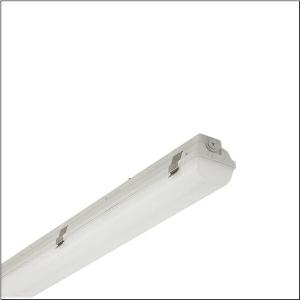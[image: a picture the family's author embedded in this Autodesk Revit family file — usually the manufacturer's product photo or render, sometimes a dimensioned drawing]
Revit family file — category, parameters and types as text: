
# Revit family: monsun_r__21_eco_51fj20ml45a_05e8
name_source: partatom
category: Lighting Fixtures
units: mm (PartAtom-declared; Revit-internal decimal feet)

## family parameters
Cut with Voids When Loaded = No
Host = Face
Light Source = No
Part Type = Normal
Room Calculation Point = No
Round Connector Dimension = Use Diameter
Shared = No

## types (1)
- --- (1 x LED, 4900 lm, 36 W, 4000K)
    Apparent Load = 36 VA
    CIE Flux Codes = 40 69 88 88 100
    Color Rendering = 80
    Color Temperature = 4000K
    Default Elevation = 1800 mm
    Description = Monsun® 21 Eco, damp-proof luminaire, primary optical cover: diffuser, of PC, UV-stabilised, frosted, light emission: direct distribution, primary light characteristic: symmetric, installation type: suspended mounting, surface-mounted, LED, rated luminous flux: 4.900lm, luminous efficacy: 132lm/W, light colour: 840, colour temperature: 4000K, control gear: ECG Multilumen, with terminal, 3-pole, max. 2.5mm², mains connection: 220..240V, AC, 50/60Hz, rated input power: 36W, housing, of glass-fibre reinforced polyester, light grey (RAL 7035), length: 1.277mm, width: 90mm, height: 95mm, clip for enclosure, of spring steel V2A, protection rating (complete): IP66, insulation class (complete): insulation class I (protective earthing), certification: CE, UKCA, protection symbol: D, impact resistance: IK08, permissible operating ambient temperature: -20..+35°C, corresponds to IFS (International Featured Standards) requirements for safety and quality in the food industry, contact your sales advisor before using the luminaires in applications with unclear chemical exposure, large temperature fluctuations or condensation-forming humidity, packaging unit: 1 piece
    Height = 103 mm
    Lamp = 1 x LED
    Lamp Light Flux = 4900 lm
    Lamp Power = 36 W
    Lamp count = 1
    Length = 1277 mm
    Luminous efficacy = 136 lm/W
    Manufacturer = Siteco
    ModVariant = No
    Model = 51FJ20ML45A
    Mounting Place = Ceiling
    Mounting Type = Surface mounted
    Number of Poles = 1
    OnlyDefault = Yes
    Power Factor = 1
    Product Name = Monsun® 21 Eco
    Product group = damp-proof luminaire
    ProductGroupID = 300
    Protection Class = Protection class I
    Protection Degree = IP 66
    RLX_Detail_Level = 1
    RLX_Emergency_Light_Flux = 0 lm
    RLX_Emergency_Type = 0
    RLX_Emergency_Type_DB = No
    RlxData = <blob elided: 34073 chars, md5=302ca06b>
    Socket = socket
    Standby Power = 0 W
    System Light Flux = 4900 lm
    System Power = 36 W
    Type Comments = factory setting: luminous flux: 100 % | (ON | ON) | 350 mA
    Type Image = l_1007218.jpg
    URL = http://relux.com
    VarID = @adj_077805
    Voltage = 0 V
    Weight = 0.00 kg
    Width = 90 mm

## geometry (parser evidence)
native form markers: Blend x4, Sweep x11
no freeform markers — native parametric forms only
